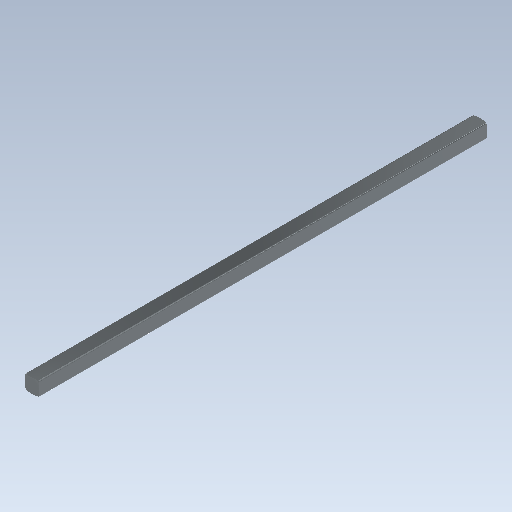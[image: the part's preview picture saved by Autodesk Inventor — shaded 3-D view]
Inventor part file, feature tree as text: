
AUTODESK INVENTOR PART (.ipt)
format: ipt  version: 2020 (Build 240168000, 168)  size: 158,720 bytes
history: native  units: in
note: dims shown in document units (in); Inventor stores cm internally (conversion verified against a paired STEP export)
features: sketch x2, plane x2, extrude x1, revolve x1, mirror x1, other x1
ambient origin geometry x8: Origin, YZ Plane, XZ Plane, XY Plane, X Axis, Y Axis, Z Axis, Center Point
bodies: Solid1 (feature_tree)
feature tree (8):
  sketch  "Sketch1"  dims[d0=4.0in d1=0.0in d2=90.0deg]
  extrude  "Extrusion1"  TaperAngle=90.0deg  [1 undecoded]
  plane  "Work Plane1"
  revolve  "Revolution1"  [1 undecoded]
  plane  "Work Plane2"
  mirror  "Mirror1"
  other  "Work Axis1"
  sketch  "Sketch2"  dims[d3=90.0deg]
note: 2 required parameter values undecoded (feature->parameter linkage not recoverable at this tier; creation-order binding heuristic only, values carry confidence <= 0.55)
